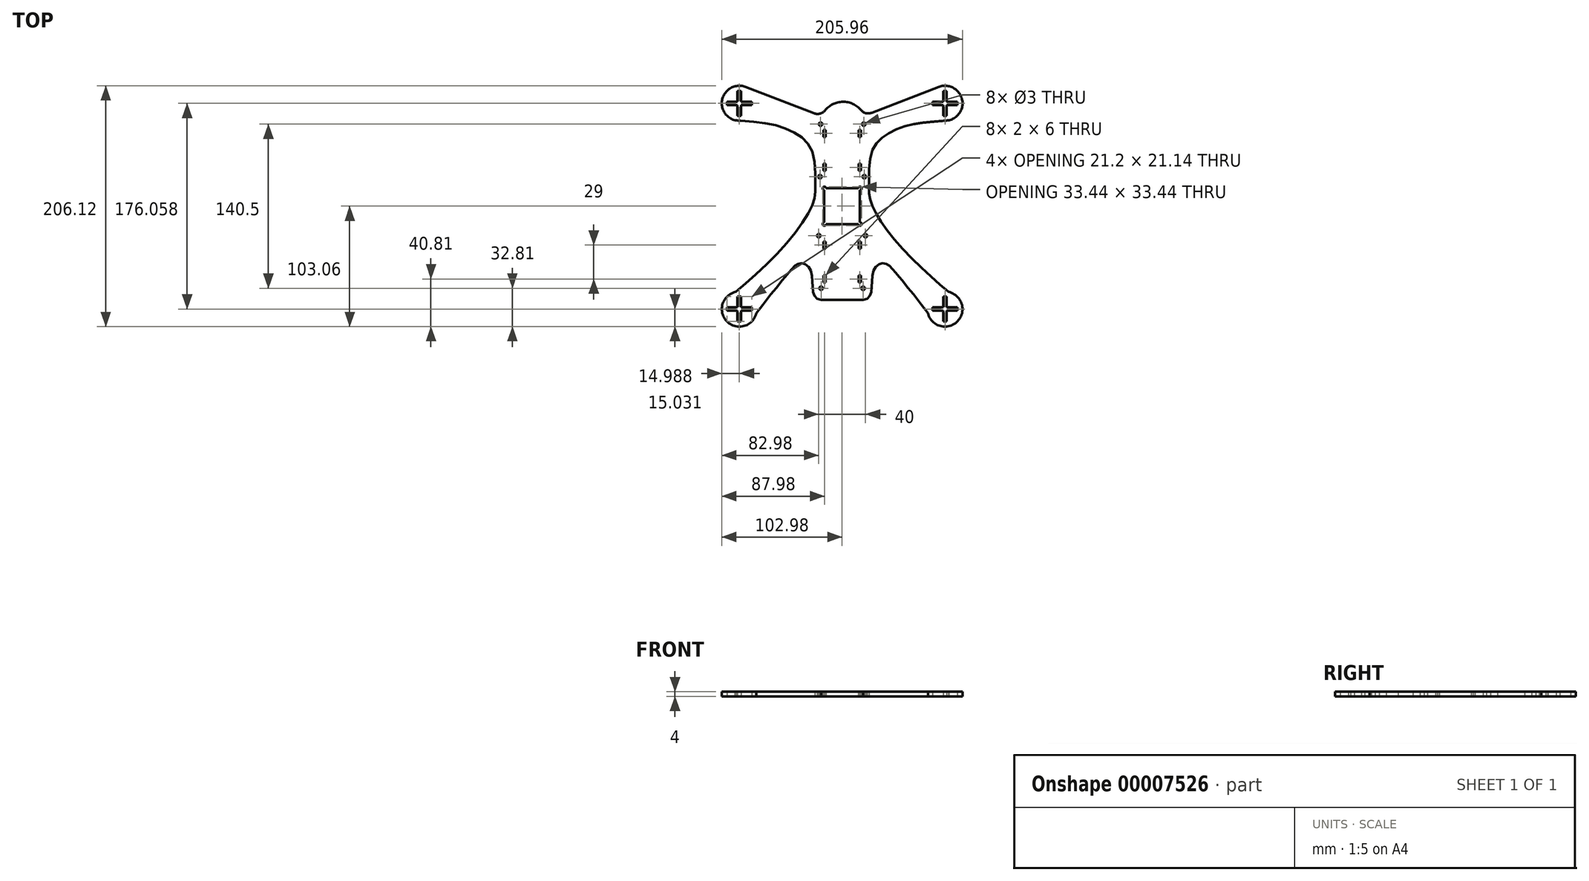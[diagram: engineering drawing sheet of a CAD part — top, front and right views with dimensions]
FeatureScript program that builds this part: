
annotation { "Feature Type Name" : "Feature", "Feature Type Description" : "" }
export const myFeature = defineFeature(function(context is Context, id is Id, definition is map)
    precondition{}
    {
        {
            var Q0;
            Q0=qCreatedBy(makeId("Top.planeOp"),FACE);
            var sketch = newSketch(context, id + "F0", { "sketchPlane" : qUnion([Q0])});
            skLineSegment(sketch, "E0.top", {"start": v(0, 110) * mm, "end": v(-110, 110) * mm});
            skLineSegment(sketch, "E0.left", {"start": v(0, 0) * mm, "end": v(0, 110) * mm});
            skLineSegment(sketch, "E0.right", {"start": v(-110, 0) * mm, "end": v(-110, 110) * mm});
            skLineSegment(sketch, "E1.top", {"start": v(0, -110) * mm, "end": v(-110, -110) * mm});
            skLineSegment(sketch, "E1.left", {"start": v(0, 0) * mm, "end": v(0, -110) * mm});
            skLineSegment(sketch, "E1.right", {"start": v(-110, 0) * mm, "end": v(-110, -110) * mm});
            skLineSegment(sketch, "E2.bottom", {"start": v(-110, -110) * mm, "end": v(-78.57, -110) * mm});
            skLineSegment(sketch, "E3.top", {"start": v(0, 110) * mm, "end": v(110, 110) * mm});
            skLineSegment(sketch, "E3.right", {"start": v(110, 0) * mm, "end": v(110, 110) * mm});
            skLineSegment(sketch, "E4.top", {"start": v(0, -110) * mm, "end": v(110, -110) * mm});
            skLineSegment(sketch, "E4.right", {"start": v(110, 0) * mm, "end": v(110, -110) * mm});
            skLineSegment(sketch, "E5.left", {"start": v(0, 0) * mm, "end": v(0, 85.41) * mm});
            skLineSegment(sketch, "E6.top", {"start": v(-88.03, 77.46) * mm, "end": v(-89.53, 77.46) * mm});
            skLineSegment(sketch, "E6.right", {"start": v(-89.53, 88.06) * mm, "end": v(-89.53, 77.46) * mm});
            skLineSegment(sketch, "E7.MirrorCS", {"start": v(-86.53, 88.07) * mm, "end": v(-86.53, 77.46) * mm});
            skLineSegment(sketch, "E8.MirrorCS", {"start": v(-88.03, 77.46) * mm, "end": v(-86.53, 77.46) * mm});
            skLineSegment(sketch, "E9.MirrorCS", {"start": v(-88, 98.6) * mm, "end": v(-89.55, 98.6) * mm});
            skLineSegment(sketch, "E10.MirrorCS", {"start": v(-88, 98.6) * mm, "end": v(-86.45, 98.6) * mm});
            skLineSegment(sketch, "E11.MirrorCS", {"start": v(-86.53, 88.07) * mm, "end": v(-86.53, 98.67) * mm});
            skLineSegment(sketch, "E12.MirrorCS", {"start": v(-89.53, 88.06) * mm, "end": v(-89.53, 98.66) * mm});
            skLineSegment(sketch, "E13.top", {"start": v(-77.4, 87.94) * mm, "end": v(-77.4, 86.44) * mm});
            skLineSegment(sketch, "E13.right", {"start": v(-98.6, 86.44) * mm, "end": v(-77.4, 86.44) * mm});
            skLineSegment(sketch, "E14.MirrorCS", {"start": v(-88, 89.44) * mm, "end": v(-77.4, 89.44) * mm});
            skLineSegment(sketch, "E15.MirrorCS", {"start": v(-77.4, 87.94) * mm, "end": v(-77.4, 89.44) * mm});
            skLineSegment(sketch, "E16.MirrorCS", {"start": v(-98.6, 87.9) * mm, "end": v(-98.6, 86.44) * mm});
            skLineSegment(sketch, "E17.MirrorCS", {"start": v(-98.6, 87.9) * mm, "end": v(-98.6, 89.44) * mm});
            skLineSegment(sketch, "E18.MirrorCS", {"start": v(-88, 89.44) * mm, "end": v(-98.6, 89.44) * mm});
            skLineSegment(sketch, "E19.bottom", {"start": v(15.25, 15.25) * mm, "end": v(-15.25, 15.25) * mm});
            skLineSegment(sketch, "E19.top", {"start": v(15.25, -15.25) * mm, "end": v(-15.25, -15.25) * mm});
            skLineSegment(sketch, "E19.left", {"start": v(15.25, 15.25) * mm, "end": v(15.25, -15.25) * mm});
            skLineSegment(sketch, "E19.right", {"start": v(-15.25, 15.25) * mm, "end": v(-15.25, -15.25) * mm});
            skPoint(sketch, "E19.middle", {"position": v(0, 0) * mm});
            skCircle(sketch, "E20", {"center": v(-15.25, 15.25) * mm, "radius": 1.5 * mm});
            skCircle(sketch, "E21", {"center": v(-15.25, -15.25) * mm, "radius": 1.5 * mm});
            skCircle(sketch, "E22", {"center": v(15.25, -15.25) * mm, "radius": 1.5 * mm});
            skCircle(sketch, "E23", {"center": v(15.25, 15.25) * mm, "radius": 1.5 * mm});
            skLineSegment(sketch, "E24", {"start": v(-54.92, 70.25) * mm, "end": v(72.97, 70.25) * mm});
            skLineSegment(sketch, "E25.bottom", {"start": v(-14, 65.25) * mm, "end": v(-16, 65.25) * mm});
            skLineSegment(sketch, "E25.top", {"start": v(-14, 59.25) * mm, "end": v(-16, 59.25) * mm});
            skLineSegment(sketch, "E25.left", {"start": v(-14, 65.25) * mm, "end": v(-14, 59.25) * mm});
            skLineSegment(sketch, "E25.right", {"start": v(-16, 65.25) * mm, "end": v(-16, 59.25) * mm});
            skCircle(sketch, "E26", {"center": v(-18.5, 70.25) * mm, "radius": 1.5 * mm});
            skCircle(sketch, "E27.MirrorC", {"center": v(18.5, 70.25) * mm, "radius": 1.5 * mm});
            skLineSegment(sketch, "E28.MirrorCS", {"start": v(14, 59.25) * mm, "end": v(16, 59.25) * mm});
            skLineSegment(sketch, "E29.MirrorCS", {"start": v(14, 65.25) * mm, "end": v(16, 65.25) * mm});
            skLineSegment(sketch, "E30.MirrorCS", {"start": v(16, 65.25) * mm, "end": v(16, 59.25) * mm});
            skLineSegment(sketch, "E31.MirrorCS", {"start": v(14, 65.25) * mm, "end": v(14, 59.25) * mm});
            skCircle(sketch, "E32", {"center": v(-19, 25.25) * mm, "radius": 1.5 * mm});
            skLineSegment(sketch, "E33.bottom", {"start": v(-14, 36.25) * mm, "end": v(-16, 36.25) * mm});
            skLineSegment(sketch, "E33.top", {"start": v(-14, 30.25) * mm, "end": v(-16, 30.25) * mm});
            skLineSegment(sketch, "E33.left", {"start": v(-14, 36.25) * mm, "end": v(-14, 30.25) * mm});
            skLineSegment(sketch, "E33.right", {"start": v(-16, 36.25) * mm, "end": v(-16, 30.25) * mm});
            skLineSegment(sketch, "E34.MirrorCS", {"start": v(14, 30.25) * mm, "end": v(16, 30.25) * mm});
            skLineSegment(sketch, "E35.MirrorCS", {"start": v(14, 36.25) * mm, "end": v(14, 30.25) * mm});
            skLineSegment(sketch, "E36.MirrorCS", {"start": v(14, 36.25) * mm, "end": v(16, 36.25) * mm});
            skLineSegment(sketch, "E37.MirrorCS", {"start": v(16, 36.25) * mm, "end": v(16, 30.25) * mm});
            skCircle(sketch, "E38.MirrorC", {"center": v(19, 25.25) * mm, "radius": 1.5 * mm});
            skCircle(sketch, "E39", {"center": v(-20, -25.25) * mm, "radius": 1.5 * mm});
            skCircle(sketch, "E40", {"center": v(-18, -70.25) * mm, "radius": 1.5 * mm});
            skCircle(sketch, "E41.MirrorC", {"center": v(20, -25.25) * mm, "radius": 1.5 * mm});
            skCircle(sketch, "E42.MirrorC", {"center": v(18, -70.25) * mm, "radius": 1.5 * mm});
            skLineSegment(sketch, "E43.MirrorCS", {"start": v(14, -30.25) * mm, "end": v(16, -30.25) * mm});
            skLineSegment(sketch, "E44.MirrorCS", {"start": v(14, -65.25) * mm, "end": v(16, -65.25) * mm});
            skLineSegment(sketch, "E45.MirrorCS", {"start": v(-14, -65.25) * mm, "end": v(-16, -65.25) * mm});
            skLineSegment(sketch, "E46.MirrorCS", {"start": v(-14, -36.25) * mm, "end": v(-16, -36.25) * mm});
            skLineSegment(sketch, "E47.MirrorCS", {"start": v(-14, -30.25) * mm, "end": v(-16, -30.25) * mm});
            skLineSegment(sketch, "E48.MirrorCS", {"start": v(14, -36.25) * mm, "end": v(16, -36.25) * mm});
            skLineSegment(sketch, "E49.MirrorCS", {"start": v(14, -59.25) * mm, "end": v(16, -59.25) * mm});
            skLineSegment(sketch, "E50.MirrorCS", {"start": v(-14, -59.25) * mm, "end": v(-16, -59.25) * mm});
            skLineSegment(sketch, "E51.MirrorCS", {"start": v(16, -36.25) * mm, "end": v(16, -30.25) * mm});
            skLineSegment(sketch, "E52.MirrorCS", {"start": v(14, -36.25) * mm, "end": v(14, -30.25) * mm});
            skLineSegment(sketch, "E53.MirrorCS", {"start": v(-14, -65.25) * mm, "end": v(-14, -59.25) * mm});
            skLineSegment(sketch, "E54.MirrorCS", {"start": v(0, 0) * mm, "end": v(0, -85.41) * mm});
            skLineSegment(sketch, "E55.MirrorCS", {"start": v(16, -65.25) * mm, "end": v(16, -59.25) * mm});
            skLineSegment(sketch, "E56.MirrorCS", {"start": v(-16, -36.25) * mm, "end": v(-16, -30.25) * mm});
            skLineSegment(sketch, "E57.MirrorCS", {"start": v(14, -65.25) * mm, "end": v(14, -59.25) * mm});
            skLineSegment(sketch, "E58.MirrorCS", {"start": v(-14, -36.25) * mm, "end": v(-14, -30.25) * mm});
            skLineSegment(sketch, "E59.MirrorCS", {"start": v(-16, -65.25) * mm, "end": v(-16, -59.25) * mm});
            skPoint(sketch, "E60.first.point", {"position": v(-98.61, 98.67) * mm});
            skPoint(sketch, "E60.third.point.positionSnap0", {"position": v(-93.3, 89.44) * mm});
            skCircle(sketch, "E61", {"center": v(-87.98, 88.06) * mm, "radius": 15 * mm});
            skCircle(sketch, "E62.MirrorC", {"center": v(87.98, 88.06) * mm, "radius": 15 * mm});
            skCircle(sketch, "E63.MirrorC", {"center": v(87.98, -88.06) * mm, "radius": 15 * mm});
            skCircle(sketch, "E64.MirrorC", {"center": v(-87.98, -88.06) * mm, "radius": 15 * mm});
            skPoint(sketch, "E65.visualSharp", {"position": v(-20.5, 25.11) * mm});
            skPoint(sketch, "E66.visualSharp", {"position": v(-21.5, -25.39) * mm});
            skLineSegment(sketch, "E67", {"start": v(-23.86, 79.44) * mm, "end": v(-82.59, 102.06) * mm});
            skPoint(sketch, "E68.visualSharp", {"position": v(0, 15.25) * mm});
            skLineSegment(sketch, "E68.filletArc", {"start": v(0, 15.25) * mm, "end": v(0, 15.25) * mm});
            skLineSegment(sketch, "E69.MirrorCS", {"start": v(25.13, 79.93) * mm, "end": v(82.59, 102.06) * mm});
            skLineSegment(sketch, "E70", {"start": v(-18, -70.25) * mm, "end": v(-18, -80.25) * mm});
            skPoint(sketch, "E71.visualSharp", {"position": v(-18, -80.25) * mm});
            skPoint(sketch, "E72.visualSharp", {"position": v(0, 70.25) * mm});
            skFitSpline(sketch, "E73", {"points": [v(-90.84, -73.34) * mm, v(-56.88, -42.02) * mm, v(-31.34, -10.16) * mm, v(-23.7, 6.68) * mm, v(-22.92, 18.8) * mm, v(-25.29, 45.9) * mm, v(-36.6, 60.38) * mm, v(-57.14, 69.33) * mm, v(-91.72, 73.54) * mm], "startDerivative": vector(171.74, 150.17) * mm, "endDerivative": vector(-302.33, 27.57) * mm});
            skFitSpline(sketch, "E74", {"points": [v(-18, -80.25) * mm, v(-24.83, -73.22) * mm, v(-27.43, -53.86) * mm, v(-35.81, -48.83) * mm, v(-45.3, -56.28) * mm, v(-56.1, -69.5) * mm, v(-73.41, -91.65) * mm], "startDerivative": vector(-99.08, 13.73) * mm, "endDerivative": vector(-146.55, -193.73) * mm});
            skLineSegment(sketch, "E75", {"start": v(-18, -80.25) * mm, "end": v(0, -80.25) * mm});
            skFitSpline(sketch, "E76.MirrorCS", {"points": [v(90.84, -73.34) * mm, v(56.88, -42.02) * mm, v(31.34, -10.16) * mm, v(23.7, 6.68) * mm, v(22.92, 18.8) * mm, v(25.29, 45.9) * mm, v(36.6, 60.38) * mm, v(57.14, 69.33) * mm, v(91.72, 73.54) * mm], "startDerivative": vector(-171.74, 150.17) * mm, "endDerivative": vector(302.33, 27.57) * mm});
            skFitSpline(sketch, "E77.MirrorCS", {"points": [v(18, -80.25) * mm, v(24.83, -73.22) * mm, v(27.43, -53.86) * mm, v(35.81, -48.83) * mm, v(45.3, -56.28) * mm, v(56.1, -69.5) * mm, v(73.41, -91.65) * mm], "startDerivative": vector(99.08, 13.73) * mm, "endDerivative": vector(146.55, -193.73) * mm});
            skLineSegment(sketch, "E78.MirrorCS", {"start": v(18, -80.25) * mm, "end": v(0, -80.25) * mm});
            skLineSegment(sketch, "E79.MirrorCS", {"start": v(98.6, 86.44) * mm, "end": v(77.4, 86.44) * mm});
            skLineSegment(sketch, "E80.MirrorCS", {"start": v(88, 89.44) * mm, "end": v(77.4, 89.44) * mm});
            skLineSegment(sketch, "E81.MirrorCS", {"start": v(77.4, 87.94) * mm, "end": v(77.4, 89.44) * mm});
            skLineSegment(sketch, "E82.MirrorCS", {"start": v(77.4, 87.94) * mm, "end": v(77.4, 86.44) * mm});
            skLineSegment(sketch, "E83.MirrorCS", {"start": v(86.53, 88.07) * mm, "end": v(86.53, 98.67) * mm});
            skLineSegment(sketch, "E84.MirrorCS", {"start": v(89.53, 88.06) * mm, "end": v(89.53, 98.66) * mm});
            skLineSegment(sketch, "E85.MirrorCS", {"start": v(88, 98.6) * mm, "end": v(86.45, 98.6) * mm});
            skLineSegment(sketch, "E86.MirrorCS", {"start": v(88, 98.6) * mm, "end": v(89.55, 98.6) * mm});
            skLineSegment(sketch, "E87.MirrorCS", {"start": v(88, 89.44) * mm, "end": v(98.6, 89.44) * mm});
            skLineSegment(sketch, "E88.MirrorCS", {"start": v(98.6, 87.9) * mm, "end": v(98.6, 89.44) * mm});
            skLineSegment(sketch, "E89.MirrorCS", {"start": v(98.6, 87.9) * mm, "end": v(98.6, 86.44) * mm});
            skLineSegment(sketch, "E90.MirrorCS", {"start": v(89.53, 88.06) * mm, "end": v(89.53, 77.46) * mm});
            skLineSegment(sketch, "E91.MirrorCS", {"start": v(86.53, 88.07) * mm, "end": v(86.53, 77.46) * mm});
            skLineSegment(sketch, "E92.MirrorCS", {"start": v(88.03, 77.46) * mm, "end": v(89.53, 77.46) * mm});
            skLineSegment(sketch, "E93.MirrorCS", {"start": v(88.03, 77.46) * mm, "end": v(86.53, 77.46) * mm});
            skLineSegment(sketch, "E94.MirrorCS", {"start": v(-89.53, -88.06) * mm, "end": v(-89.53, -77.46) * mm});
            skLineSegment(sketch, "E95.MirrorCS", {"start": v(-86.53, -88.07) * mm, "end": v(-86.53, -77.46) * mm});
            skLineSegment(sketch, "E96.MirrorCS", {"start": v(-88.03, -77.46) * mm, "end": v(-89.53, -77.46) * mm});
            skLineSegment(sketch, "E97.MirrorCS", {"start": v(-88.03, -77.46) * mm, "end": v(-86.53, -77.46) * mm});
            skLineSegment(sketch, "E98.MirrorCS", {"start": v(-98.6, -86.44) * mm, "end": v(-77.4, -86.44) * mm});
            skLineSegment(sketch, "E99.MirrorCS", {"start": v(-77.4, -87.94) * mm, "end": v(-77.4, -86.44) * mm});
            skLineSegment(sketch, "E100.MirrorCS", {"start": v(-77.4, -87.94) * mm, "end": v(-77.4, -89.44) * mm});
            skLineSegment(sketch, "E101.MirrorCS", {"start": v(-88, -89.44) * mm, "end": v(-77.4, -89.44) * mm});
            skLineSegment(sketch, "E102.MirrorCS", {"start": v(-86.53, -88.07) * mm, "end": v(-86.53, -98.67) * mm});
            skLineSegment(sketch, "E103.MirrorCS", {"start": v(-88, -98.6) * mm, "end": v(-86.45, -98.6) * mm});
            skLineSegment(sketch, "E104.MirrorCS", {"start": v(-88, -98.6) * mm, "end": v(-89.55, -98.6) * mm});
            skLineSegment(sketch, "E105.MirrorCS", {"start": v(-88, -89.44) * mm, "end": v(-98.6, -89.44) * mm});
            skLineSegment(sketch, "E106.MirrorCS", {"start": v(-98.6, -87.9) * mm, "end": v(-98.6, -89.44) * mm});
            skLineSegment(sketch, "E107.MirrorCS", {"start": v(-98.6, -87.9) * mm, "end": v(-98.6, -86.44) * mm});
            skLineSegment(sketch, "E108.MirrorCS", {"start": v(-89.53, -88.06) * mm, "end": v(-89.53, -98.66) * mm});
            skLineSegment(sketch, "E109.MirrorCS", {"start": v(98.6, -86.44) * mm, "end": v(77.4, -86.44) * mm});
            skLineSegment(sketch, "E110.MirrorCS", {"start": v(88, -89.44) * mm, "end": v(77.4, -89.44) * mm});
            skLineSegment(sketch, "E111.MirrorCS", {"start": v(86.53, -88.07) * mm, "end": v(86.53, -98.67) * mm});
            skLineSegment(sketch, "E112.MirrorCS", {"start": v(89.53, -88.06) * mm, "end": v(89.53, -98.66) * mm});
            skLineSegment(sketch, "E113.MirrorCS", {"start": v(88, -89.44) * mm, "end": v(98.6, -89.44) * mm});
            skLineSegment(sketch, "E114.MirrorCS", {"start": v(89.53, -88.06) * mm, "end": v(89.53, -77.46) * mm});
            skLineSegment(sketch, "E115.MirrorCS", {"start": v(86.53, -88.07) * mm, "end": v(86.53, -77.46) * mm});
            skLineSegment(sketch, "E116.MirrorCS", {"start": v(88.03, -77.46) * mm, "end": v(89.53, -77.46) * mm});
            skLineSegment(sketch, "E117.MirrorCS", {"start": v(88.03, -77.46) * mm, "end": v(86.53, -77.46) * mm});
            skLineSegment(sketch, "E118.MirrorCS", {"start": v(77.4, -87.94) * mm, "end": v(77.4, -86.44) * mm});
            skLineSegment(sketch, "E119.MirrorCS", {"start": v(77.4, -87.94) * mm, "end": v(77.4, -89.44) * mm});
            skLineSegment(sketch, "E120.MirrorCS", {"start": v(88, -98.6) * mm, "end": v(86.45, -98.6) * mm});
            skLineSegment(sketch, "E121.MirrorCS", {"start": v(88, -98.6) * mm, "end": v(89.55, -98.6) * mm});
            skLineSegment(sketch, "E122.MirrorCS", {"start": v(98.6, -87.9) * mm, "end": v(98.6, -89.44) * mm});
            skLineSegment(sketch, "E123.MirrorCS", {"start": v(98.6, -87.9) * mm, "end": v(98.6, -86.44) * mm});
            skArc(sketch, "E124", {"start": v(16.14, 82.23) * mm, "mid": v(0.6, 89.34) * mm, "end": v(-14.76, 81.89) * mm});
            skPoint(sketch, "E125.visualSharp", {"position": v(-17.64, 77.05) * mm});
            skArc(sketch, "E125.filletArc", {"start": v(-23.86, 79.44) * mm, "mid": v(-18.91, 79.18) * mm, "end": v(-14.76, 81.89) * mm});
            skPoint(sketch, "E126.visualSharp", {"position": v(19.07, 77.6) * mm});
            skArc(sketch, "E126.filletArc", {"start": v(16.14, 82.23) * mm, "mid": v(20.26, 79.64) * mm, "end": v(25.13, 79.93) * mm});
            skSolve(sketch);
        }
        {
            var Q0;
            {var subQ9=sQuery(id+"F0.wireOp",EDGE,"E96.MirrorCS");Q0=makeQuery(id+"F0.imprint","IMPRINT",FACE,{"disambiguationData":[TD([[makeQuery(id+"F0.imprint","IMPRINT",EDGE,{"derivedFrom":subQ9}),-1.0]])]});}
            var Q1;
            Q1=makeQuery(id+"F0.imprint","IMPRINT",FACE,{"disambiguationData":[TD([[makeQuery(id+"F0.imprint","IMPRINT",EDGE,{"derivedFrom":sQuery(id+"F0.wireOp",EDGE,"E25.bottom")}),-1.0]])]});
            var Q2;
            Q2=makeQuery(id+"F0.imprint","IMPRINT",FACE,{"disambiguationData":[TD([[makeQuery(id+"F0.imprint","IMPRINT",EDGE,{"derivedFrom":sQuery(id+"F0.wireOp",EDGE,"E28.MirrorCS")}),-1.0]])]});
            var Q3;
            {var subQ22=sQuery(id+"F0.wireOp",EDGE,"E116.MirrorCS");Q3=makeQuery(id+"F0.imprint","IMPRINT",FACE,{"disambiguationData":[TD([[makeQuery(id+"F0.imprint","IMPRINT",EDGE,{"derivedFrom":subQ22}),1.0]])]});}
            var Q4;
            {var subQ12=sQuery(id+"F0.wireOp",EDGE,"E69.MirrorCS");Q4=makeQuery(id+"F0.imprint","IMPRINT",FACE,{"disambiguationData":[TD([[makeQuery(id+"F0.imprint","IMPRINT",EDGE,{"derivedFrom":subQ12}),-1.0]])]});}
            var Q5;
            {var subQ6=sQuery(id+"F0.wireOp",EDGE,"E81.MirrorCS");Q5=makeQuery(id+"F0.imprint","IMPRINT",FACE,{"disambiguationData":[TD([[makeQuery(id+"F0.imprint","IMPRINT",EDGE,{"derivedFrom":subQ6}),1.0]])]});}
            var Q6;
            {var subQ12=sQuery(id+"F0.wireOp",EDGE,"E6.top");Q6=makeQuery(id+"F0.imprint","IMPRINT",FACE,{"disambiguationData":[TD([[makeQuery(id+"F0.imprint","IMPRINT",EDGE,{"derivedFrom":subQ12}),1.0]])]});}
            var Q7;
            {var subQ0=sQuery(id+"F0.wireOp",EDGE,"E54.MirrorCS");var subQ5=sQuery(id+"F0.wireOp",EDGE,"E5.left");var subQ6=makeQuery(id+"F0.imprint","INTERSECT",VERTEX,{"derivedFrom":[subQ5,subQ0]});Q7=makeQuery(id+"F0.imprint","IMPRINT",FACE,{"disambiguationData":[TD([[makeQuery(id+"F0.imprint","IMPRINT",EDGE,{"disambiguationData":[TD([[subQ6,-1.0]])],"derivedFrom":subQ5}),1.0]])]});}
            var Q8;
            {var subQ7=sQuery(id+"F0.wireOp",EDGE,"E54.MirrorCS");var subQ8=sQuery(id+"F0.wireOp",EDGE,"E5.left");var subQ9=makeQuery(id+"F0.imprint","INTERSECT",VERTEX,{"derivedFrom":[subQ8,subQ7]});Q8=makeQuery(id+"F0.imprint","IMPRINT",FACE,{"disambiguationData":[TD([[makeQuery(id+"F0.imprint","IMPRINT",EDGE,{"disambiguationData":[TD([[subQ9,-1.0]])],"derivedFrom":subQ8}),-1.0]])]});}
            extrude(context, id + "F1", {"entities" : qUnion([Q0, Q1, Q2, Q3, Q4, Q5, Q6, Q7, Q8]), "depth" : 4 * mm, "offsetDistance" : 25 * mm});
        }
    });
